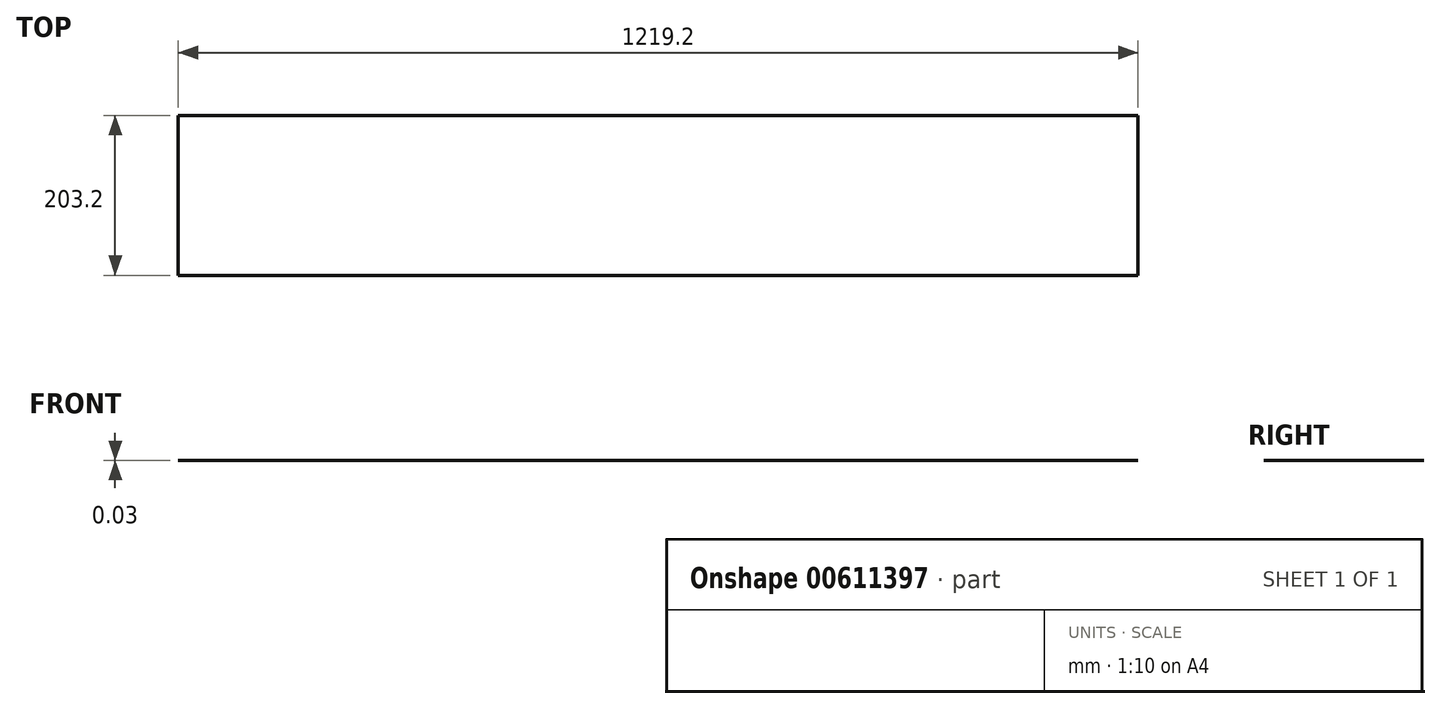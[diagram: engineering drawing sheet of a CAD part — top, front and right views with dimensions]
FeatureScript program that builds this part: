
annotation { "Feature Type Name" : "Feature", "Feature Type Description" : "" }
export const myFeature = defineFeature(function(context is Context, id is Id, definition is map)
    precondition{}
    {
        {
            var Q0;
            Q0=qCreatedBy(makeId("Top.planeOp"),FACE);
            var sketch = newSketch(context, id + "F0", { "sketchPlane" : qUnion([Q0])});
            skLineSegment(sketch, "E0.bottom", {"start": v(-609.6, 101.6) * mm, "end": v(609.6, 101.6) * mm});
            skLineSegment(sketch, "E0.top", {"start": v(-609.6, -101.6) * mm, "end": v(609.6, -101.6) * mm});
            skLineSegment(sketch, "E0.left", {"start": v(-609.6, 101.6) * mm, "end": v(-609.6, -101.6) * mm});
            skLineSegment(sketch, "E0.right", {"start": v(609.6, 101.6) * mm, "end": v(609.6, -101.6) * mm});
            skPoint(sketch, "E0.middle", {"position": v(0, 0) * mm});
            skSolve(sketch);
        }
        {
            var Q0;
            Q0 = qSketchRegion(id + "F0", true);
            extrude(context, id + "F1", {"entities" : qUnion([Q0]), "depth" : 3 / 101.6 * mm, "offsetDistance" : 25.4 * mm});
        }
    });
